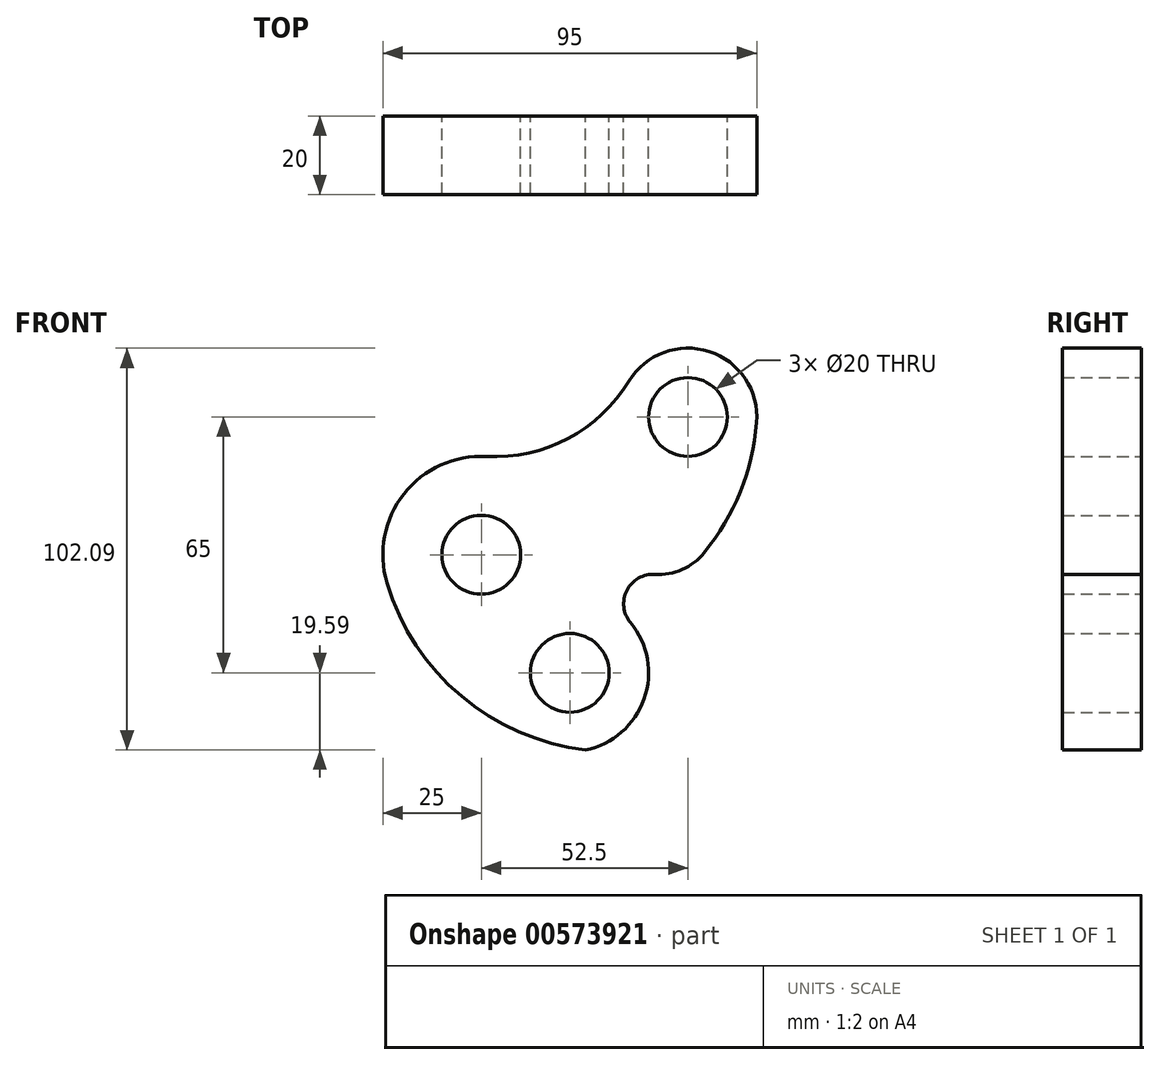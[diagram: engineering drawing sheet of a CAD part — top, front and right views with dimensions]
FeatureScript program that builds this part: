
annotation { "Feature Type Name" : "Feature", "Feature Type Description" : "" }
export const myFeature = defineFeature(function(context is Context, id is Id, definition is map)
    precondition{}
    {
        {
            var Q0;
            Q0=qCreatedBy(makeId("Front.planeOp"),FACE);
            var sketch = newSketch(context, id + "F0", { "sketchPlane" : qUnion([Q0])});
            skCircle(sketch, "E0", {"center": v(0, 0) * mm, "radius": 10 * mm});
            skArc(sketch, "E1", {"start": v(1.3, 24.97) * mm, "mid": v(-19.65, 15.46) * mm, "end": v(-23.96, -7.14) * mm});
            skCircle(sketch, "E2", {"center": v(22.5, -30) * mm, "radius": 10 * mm});
            skCircle(sketch, "E3", {"center": v(52.5, 35) * mm, "radius": 10 * mm});
            skArc(sketch, "E4", {"start": v(8.99, -44.75) * mm, "mid": v(36.28, -44.5) * mm, "end": v(37.9, -17.24) * mm});
            skArc(sketch, "E5", {"start": v(-23.96, -7.14) * mm, "mid": v(-5.07, -35.93) * mm, "end": v(26.53, -49.59) * mm});
            skArc(sketch, "E6", {"start": v(69.94, 33.58) * mm, "mid": v(57.9, 51.64) * mm, "end": v(37.55, 44.1) * mm});
            skArc(sketch, "E7", {"start": v(1.3, 24.97) * mm, "mid": v(22.07, 29.54) * mm, "end": v(37.55, 44.1) * mm});
            skArc(sketch, "E8", {"start": v(44.12, -4.97) * mm, "mid": v(37, -9.07) * mm, "end": v(37.9, -17.24) * mm});
            skArc(sketch, "E9", {"start": v(44.12, -4.97) * mm, "mid": v(51.03, -3.73) * mm, "end": v(56.62, 0.51) * mm});
            skArc(sketch, "E10", {"start": v(56.62, 0.51) * mm, "mid": v(65.8, 16.03) * mm, "end": v(69.94, 33.58) * mm});
            skSolve(sketch);
        }
        {
            var Q0;
            Q0=makeQuery(id+"F0.imprint","IMPRINT",FACE,{"disambiguationData":[TD([[makeQuery(id+"F0.imprint","IMPRINT",EDGE,{"derivedFrom":sQuery(id+"F0.wireOp",EDGE,"E0")}),-1.0]])]});
            extrude(context, id + "F1", {"entities" : qUnion([Q0]), "depth" : 20 * mm, "offsetDistance" : 25 * mm});
        }
    });
